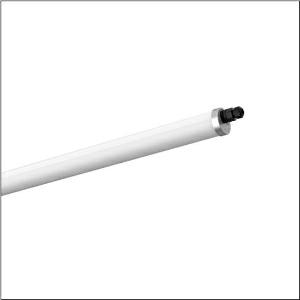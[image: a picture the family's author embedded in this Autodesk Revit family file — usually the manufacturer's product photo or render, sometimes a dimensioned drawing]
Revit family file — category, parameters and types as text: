
# Revit family: monsun_r__31_tube_51ft10dn480a_9fe9
name_source: partatom
category: Lighting Fixtures
units: mm (PartAtom-declared; Revit-internal decimal feet)

## family parameters
Cut with Voids When Loaded = No
Host = Face
Light Source = No
Part Type = Normal
Room Calculation Point = No
Round Connector Dimension = Use Diameter
Shared = No

## types (1)
- Monsun® 31 Tube (1 x LED, 8000 lm, 50 W, 4000K)
    Apparent Load = 50 VA
    CIE Flux Codes = 42 71 89 91 100
    Color Rendering = 80
    Color Temperature = 4000K
    Default Elevation = 1800 mm
    Description = Monsun® 31 Tube, tubular luminaire, primary optical cover: diffuser, of PMMA, light emission: direct distribution, primary light characteristic: symmetric, installation type: suspended mounting, surface-mounted, LED, rated luminous flux: 8.000lm, luminous efficacy: 160lm/W, light colour: 840, colour temperature: 4000K, with with 1 terminal, 5-pole, max. 2.5mm², through-wiring: 5x 1.5mm², mains connection: 220..240V, AC, 50/60Hz, rated input power: 50W, housing, cylindrical, of PMMA, semi-transparent, matt white, with luminaire and ceiling fastening, V4A, mounting with brackets of stainless steel, length: 1.570mm, diameter: 75mm, end cap, of stainless steel (V4A), protection rating (complete): IP67/IP69K, insulation class (complete): insulation class I (protective earthing), certification: CE, UKCA, impact resistance: IK07, permissible operating ambient temperature: -20..+40°C, corresponds to IFS (International Featured Standards) requirements for safety and quality in the food industry, usage in unprotected outdoor area possible with horizontal mounting, contact your sales advisor before using the luminaires in applications with unclear chemical exposure, large temperature fluctuations or condensation-forming humidity, packaging unit: 1 piece
    Height = 83 mm
    Lamp = 1 x LED
    Lamp Light Flux = 8000 lm
    Lamp Power = 50 W
    Lamp count = 1
    Length = 1570 mm
    Luminous efficacy = 160 lm/W
    Manufacturer = Siteco
    ModVariant = No
    Model = 51FT10DN480A
    Mounting Place = Ceiling
    Mounting Type = Pendant
    Number of Poles = 1
    OnlyDefault = Yes
    Power Factor = 1
    Product Name = Monsun® 31 Tube
    Product group = tubular luminaire
    ProductGroupID = 906
    Protection Class = Protection class I
    RLX_Detail_Level = 1
    RLX_Emergency_Light_Flux = 0 lm
    RLX_Emergency_Type = 0
    RLX_Emergency_Type_DB = No
    RlxData = <blob elided: 25349 chars, md5=06ae8c66>
    Socket = socket
    Standby Power = 0 W
    System Light Flux = 8000 lm
    System Power = 50 W
    Type Comments = Product without accessories
    Type Image = l_1228461.jpg
    URL = http://relux.com
    VarID = ---
    Voltage = 0 V
    Weight = 0.00 kg
    Width = 75 mm

## geometry (parser evidence)
native form markers: Blend x4, Sweep x14
no freeform markers — native parametric forms only
